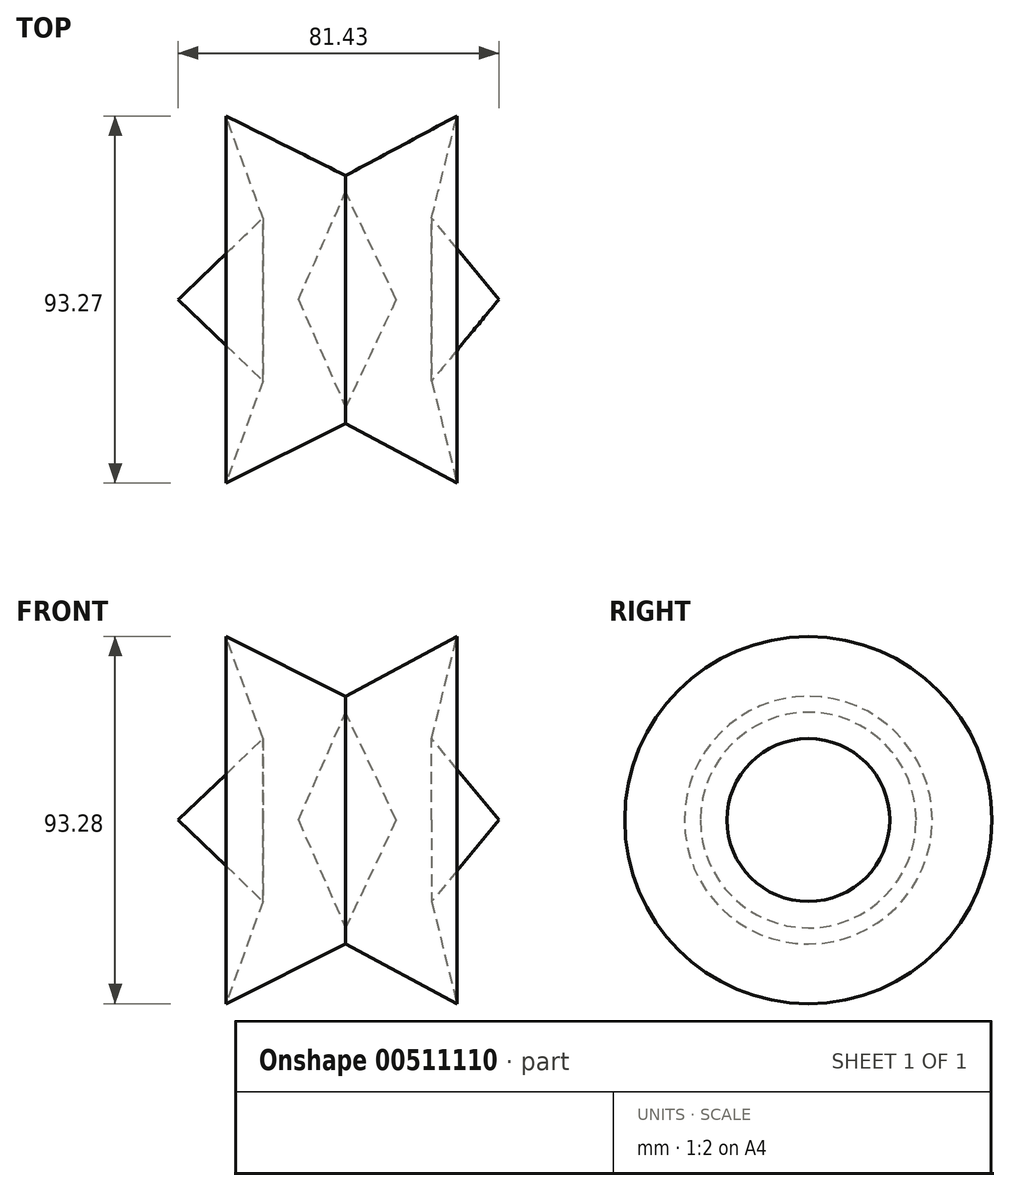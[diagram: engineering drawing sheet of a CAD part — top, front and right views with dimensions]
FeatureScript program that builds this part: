
annotation { "Feature Type Name" : "Feature", "Feature Type Description" : "" }
export const myFeature = defineFeature(function(context is Context, id is Id, definition is map)
    precondition{}
    {
        {
            var Q0;
            Q0=qCreatedBy(makeId("Top.planeOp"),FACE);
            var sketch = newSketch(context, id + "F0", { "sketchPlane" : qUnion([Q0])});
            skLineSegment(sketch, "E0", {"start": v(0, 37.16) * mm, "end": v(-11.95, 9.76) * mm});
            skLineSegment(sketch, "E1", {"start": v(-11.95, 9.76) * mm, "end": v(-42.5, 9.76) * mm});
            skLineSegment(sketch, "E2", {"start": v(-42.5, 9.76) * mm, "end": v(-20.99, -10.93) * mm});
            skLineSegment(sketch, "E3", {"start": v(-20.99, -10.93) * mm, "end": v(-30.39, -36.87) * mm});
            skLineSegment(sketch, "E4", {"start": v(-30.39, -36.87) * mm, "end": v(0, -21.71) * mm});
            skLineSegment(sketch, "E5", {"start": v(0, -21.71) * mm, "end": v(28.27, -36.87) * mm});
            skLineSegment(sketch, "E6", {"start": v(28.27, -36.87) * mm, "end": v(21.86, -10.93) * mm});
            skLineSegment(sketch, "E7", {"start": v(21.86, -10.93) * mm, "end": v(38.93, 9.76) * mm});
            skLineSegment(sketch, "E8", {"start": v(38.93, 9.76) * mm, "end": v(12.87, 9.76) * mm});
            skLineSegment(sketch, "E9", {"start": v(12.87, 9.76) * mm, "end": v(0, 37.16) * mm});
            skSolve(sketch);
        }
        {
            var Q0;
            Q0=makeQuery(id+"F0.imprint","IMPRINT",FACE,{"disambiguationData":[TD([[makeQuery(id+"F0.imprint","IMPRINT",EDGE,{"derivedFrom":sQuery(id+"F0.wireOp",EDGE,"E0")}),1.0]])]});
            var Q1;
            Q1=sQuery(id+"F0.wireOp",EDGE,"E1");
            revolve(context, id + "F1", {"entities" : qUnion([Q0]), "axis" : qUnion([Q1]), "revolveType" : RevolveType.FULL});
        }
    });
